# Revit family: Basin-Undercounter-DXV-Belshire-D20205000.415
name_source: partatom
category: Plumbing Fixtures
revit_build: Autodesk Revit 2016 (Build: 20150714_1515(x64)
units: mm (PartAtom-declared; Revit-internal decimal feet)

## family parameters
Always vertical = No
Cut with Voids When Loaded = Yes
OmniClass Number = 23.45.05.14.14
OmniClass Title = Sinks/Lavatories
Part Type = Normal
Room Calculation Point = No
Round Connector Dimension = Use Diameter
Shared = Yes
Work Plane-Based = Yes

## types (1)
- D20205000.415
    Assembly Code = D2010310
    Basin Shape = Rectangular
    CW Connection = Yes
    CWFU = 1.5
    Cold Water Connection Diameter = 3/8"
    Cold Water Connection Height = 25 1/2"
    Cold Water Connection Width = 4"
    Default Elevation = 34"
    Description = DXV BELSHIRE™ UNDERCOUNTER SINK
    Finish = Vitreous China-DXV-415-Canvas White
    HW Connection = Yes
    HWFU = 1.5
    Height = 5 1/2"
    Hot Water Connection Diameter = 0"
    Hot Water Connection Height = 25 1/2"
    Hot Water Connection Width = 4"
    Installation Type = Undermount
    Length = 14 5/8"
    Manufacturer = DXV
    Material = Vitreous China-DXV-415-Canvas White
    Model = D20205000.415
    Price = Prices may vary. Please consult Manufacturer Representative for most up-to-date price list.
    URL = https://www.dxv.com
    Vent Connection = No
    WFU = 2
    Warranty Documentation Link = https://www.dxv.com
    Waste Connection = Yes
    Waste Connection Diameter = 1 1/4"
    Waste Connection Height = 25"
    Width = 19"

## geometry (parser evidence)
native form markers: Sweep x2
no freeform markers — native parametric forms only
